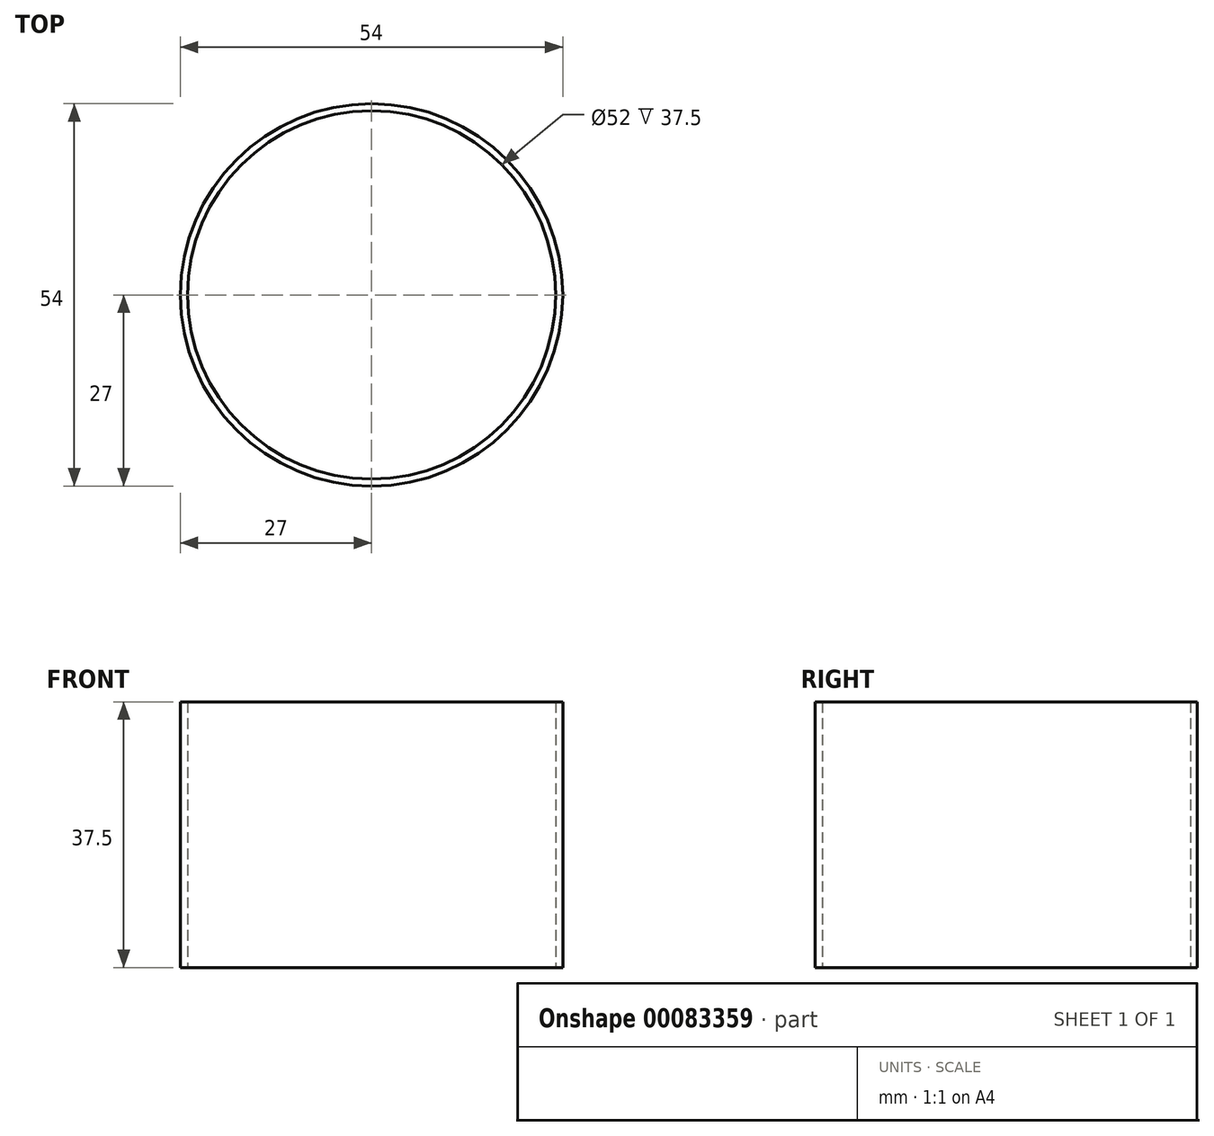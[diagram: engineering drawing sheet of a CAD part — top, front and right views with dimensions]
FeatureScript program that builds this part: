
annotation { "Feature Type Name" : "Feature", "Feature Type Description" : "" }
export const myFeature = defineFeature(function(context is Context, id is Id, definition is map)
    precondition{}
    {
        {
            var Q0;
            Q0=qCreatedBy(makeId("Top.planeOp"),FACE);
            var sketch = newSketch(context, id + "F0", { "sketchPlane" : qUnion([Q0])});
            skCircle(sketch, "E0", {"center": v(0, 0) * mm, "radius": 26 * mm});
            skCircle(sketch, "E1.0", {"center": v(0, 0) * mm, "radius": 27 * mm});
            skSolve(sketch);
        }
        {
            var Q0;
            Q0=makeQuery(id+"F0.imprint","IMPRINT",FACE,{"disambiguationData":[TD([[makeQuery(id+"F0.imprint","IMPRINT",EDGE,{"derivedFrom":sQuery(id+"F0.wireOp",EDGE,"E0")}),-1.0]])]});
            extrude(context, id + "F1", {"entities" : qUnion([Q0]), "depth" : 37.5 * mm});
        }
    });
